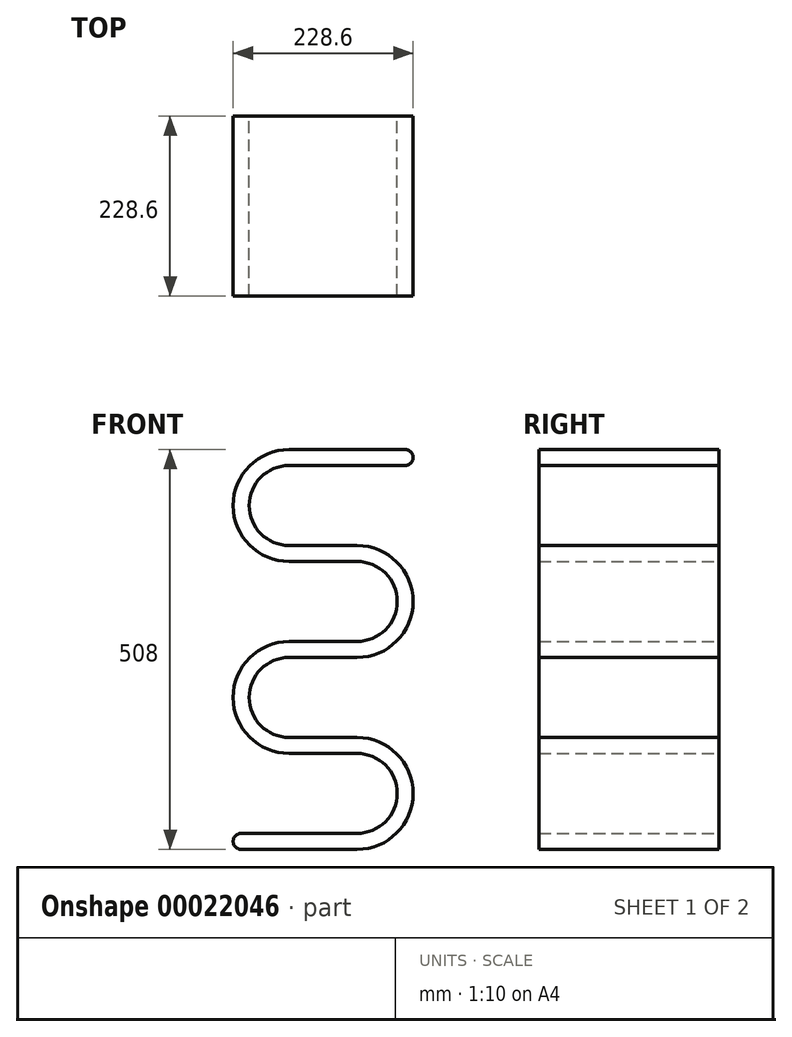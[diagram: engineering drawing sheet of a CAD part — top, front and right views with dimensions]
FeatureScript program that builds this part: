
annotation { "Feature Type Name" : "Feature", "Feature Type Description" : "" }
export const myFeature = defineFeature(function(context is Context, id is Id, definition is map)
    precondition{}
    {
        {
            var Q0;
            Q0=qCreatedBy(makeId("Front.planeOp"),FACE);
            var sketch = newSketch(context, id + "F0", { "sketchPlane" : qUnion([Q0])});
            skLineSegment(sketch, "E0.bottom", {"start": v(-27.95, 339.04) * mm, "end": v(119.37, 339.04) * mm});
            skLineSegment(sketch, "E0.top", {"start": v(-88.9, -168.96) * mm, "end": v(58.41, -168.96) * mm});
            skLineSegment(sketch, "E1", {"start": v(-27.95, 196.8) * mm, "end": v(58.41, 196.8) * mm});
            skLineSegment(sketch, "E2", {"start": v(58.41, -26.72) * mm, "end": v(-27.95, -26.72) * mm});
            skLineSegment(sketch, "E3", {"start": v(108.19, -148.64) * mm, "end": v(107.71, -148.64) * mm});
            skPoint(sketch, "E4.end.orphan", {"position": v(21.93, 318.72) * mm});
            skPoint(sketch, "E5.end.orphan", {"position": v(51.74, 196.8) * mm});
            skPoint(sketch, "E6.end.orphan", {"position": v(35.1, 217.12) * mm});
            skPoint(sketch, "E7.end.orphan", {"position": v(32.82, 95.2) * mm});
            skPoint(sketch, "E8.end.orphan", {"position": v(15.23, 74.88) * mm});
            skPoint(sketch, "E8.start.orphan", {"position": v(15.23, 95.2) * mm});
            skPoint(sketch, "E9.end.orphan", {"position": v(75.94, -26.72) * mm});
            skPoint(sketch, "E10.end.orphan", {"position": v(59.3, -47.04) * mm});
            skPoint(sketch, "E11.end.orphan", {"position": v(107.71, -148.64) * mm});
            skArc(sketch, "E12", {"start": v(-27.95, 339.04) * mm, "mid": v(-99.07, 267.92) * mm, "end": v(-27.95, 196.8) * mm});
            skArc(sketch, "E13", {"start": v(-27.95, 318.72) * mm, "mid": v(-78.75, 267.92) * mm, "end": v(-27.95, 217.12) * mm});
            skLineSegment(sketch, "E14.trimOffspring", {"start": v(-27.95, 318.72) * mm, "end": v(119.37, 318.72) * mm});
            skLineSegment(sketch, "E15.trimOffspring", {"start": v(-27.95, 217.12) * mm, "end": v(58.41, 217.12) * mm});
            skArc(sketch, "E16", {"start": v(58.41, 74.88) * mm, "mid": v(129.53, 146) * mm, "end": v(58.41, 217.12) * mm});
            skArc(sketch, "E17", {"start": v(58.41, 95.2) * mm, "mid": v(109.21, 146) * mm, "end": v(58.41, 196.8) * mm});
            skLineSegment(sketch, "E18.trimOffspring", {"start": v(58.41, 95.2) * mm, "end": v(-27.95, 95.2) * mm});
            skArc(sketch, "E19", {"start": v(-27.95, 95.2) * mm, "mid": v(-99.07, 24.08) * mm, "end": v(-27.95, -47.04) * mm});
            skArc(sketch, "E20", {"start": v(-27.95, 74.88) * mm, "mid": v(-78.75, 24.08) * mm, "end": v(-27.95, -26.72) * mm});
            skLineSegment(sketch, "E21.trimOffspring", {"start": v(-27.95, 74.88) * mm, "end": v(58.41, 74.88) * mm});
            skArc(sketch, "E22", {"start": v(58.41, -168.96) * mm, "mid": v(129.53, -97.84) * mm, "end": v(58.41, -26.72) * mm});
            skArc(sketch, "E23", {"start": v(58.41, -148.64) * mm, "mid": v(109.21, -97.84) * mm, "end": v(58.41, -47.04) * mm});
            skLineSegment(sketch, "E24.trimOffspring", {"start": v(59.3, -47.04) * mm, "end": v(-27.95, -47.04) * mm});
            skArc(sketch, "E25", {"start": v(119.37, 318.72) * mm, "mid": v(129.53, 328.88) * mm, "end": v(119.37, 339.04) * mm});
            skArc(sketch, "E26", {"start": v(-88.9, -148.64) * mm, "mid": v(-99.07, -158.8) * mm, "end": v(-88.9, -168.96) * mm});
            skPoint(sketch, "E27.orphan", {"position": v(-99.07, 318.72) * mm});
            skPoint(sketch, "E28.start.orphan", {"position": v(-99.07, 217.12) * mm});
            skPoint(sketch, "E29.orphan", {"position": v(-99.07, 196.8) * mm});
            skPoint(sketch, "E30.orphan", {"position": v(-99.07, 95.2) * mm});
            skPoint(sketch, "E31.orphan", {"position": v(129.53, 95.2) * mm});
            skPoint(sketch, "E32.orphan", {"position": v(129.53, -26.72) * mm});
            skPoint(sketch, "E33.left.start.orphan", {"position": v(129.53, -47.04) * mm});
            skPoint(sketch, "E34.trimOffspring.start.orphan", {"position": v(129.53, -148.64) * mm});
            skPoint(sketch, "E35.left.start.orphan", {"position": v(-99.07, 74.88) * mm});
            skLineSegment(sketch, "E36.trimOffspring", {"start": v(58.41, -148.64) * mm, "end": v(-88.9, -148.64) * mm});
            skSolve(sketch);
        }
        {
            var Q0;
            Q0 = qSketchRegion(id + "F0", true);
            extrude(context, id + "F1", {"entities" : qUnion([Q0]), "depth" : 228.6 * mm});
        }
    });
